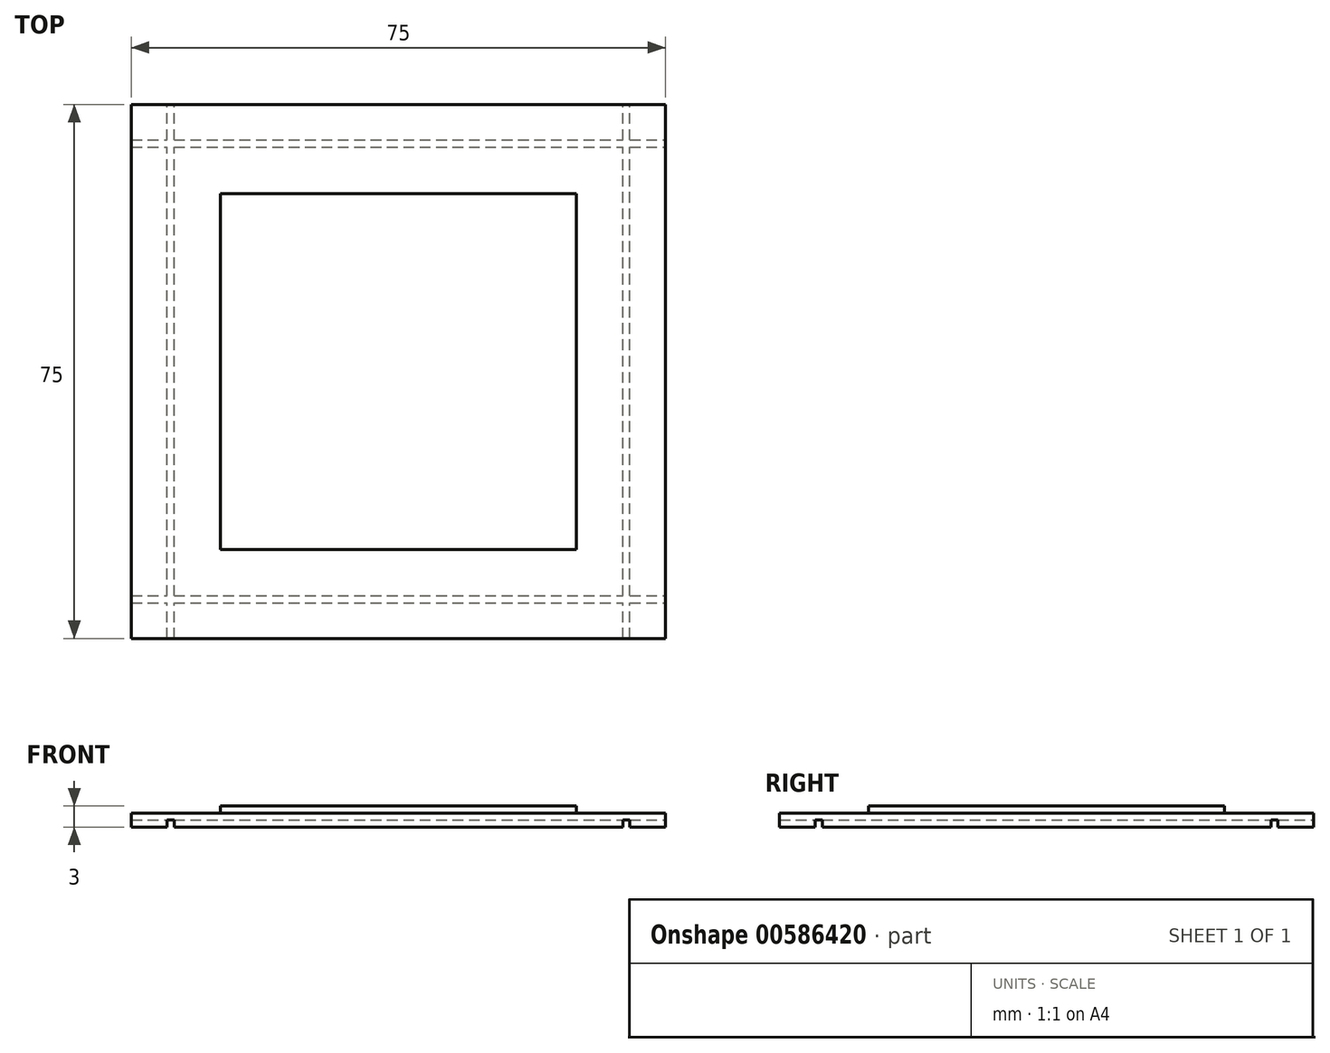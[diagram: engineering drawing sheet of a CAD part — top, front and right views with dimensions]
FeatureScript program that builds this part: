
annotation { "Feature Type Name" : "Feature", "Feature Type Description" : "" }
export const myFeature = defineFeature(function(context is Context, id is Id, definition is map)
    precondition{}
    {
        {
            var Q0;
            Q0=qCreatedBy(makeId("Top.planeOp"),FACE);
            var sketch = newSketch(context, id + "F0", { "sketchPlane" : qUnion([Q0])});
            skLineSegment(sketch, "E0.bottom", {"start": v(-37.5, -37.5) * mm, "end": v(37.5, -37.5) * mm});
            skLineSegment(sketch, "E0.top", {"start": v(-37.5, 37.5) * mm, "end": v(37.5, 37.5) * mm});
            skLineSegment(sketch, "E0.left", {"start": v(-37.5, -37.5) * mm, "end": v(-37.5, 37.5) * mm});
            skLineSegment(sketch, "E0.right", {"start": v(37.5, -37.5) * mm, "end": v(37.5, 37.5) * mm});
            skPoint(sketch, "E0.middle", {"position": v(0, 0) * mm});
            skLineSegment(sketch, "E1.bottom", {"start": v(-25, -25) * mm, "end": v(25, -25) * mm});
            skLineSegment(sketch, "E1.top", {"start": v(-25, 25) * mm, "end": v(25, 25) * mm});
            skLineSegment(sketch, "E1.left", {"start": v(-25, -25) * mm, "end": v(-25, 25) * mm});
            skLineSegment(sketch, "E1.right", {"start": v(25, -25) * mm, "end": v(25, 25) * mm});
            skSolve(sketch);
        }
        {
            var Q0;
            Q0=makeQuery(id+"F0.imprint","IMPRINT",FACE,{"disambiguationData":[TD([[makeQuery(id+"F0.imprint","IMPRINT",EDGE,{"derivedFrom":sQuery(id+"F0.wireOp",EDGE,"E1.bottom")}),1.0]])]});
            var Q1;
            Q1=makeQuery(id+"F0.imprint","IMPRINT",FACE,{"disambiguationData":[TD([[makeQuery(id+"F0.imprint","IMPRINT",EDGE,{"derivedFrom":sQuery(id+"F0.wireOp",EDGE,"E0.bottom")}),1.0]])]});
            extrude(context, id + "F1", {"entities" : qUnion([Q0, Q1]), "depth" : 2 * mm, "offsetDistance" : 25 * mm});
        }
        {
            var Q0;
            Q0=makeQuery(id+"F0.imprint","IMPRINT",FACE,{"disambiguationData":[TD([[makeQuery(id+"F0.imprint","IMPRINT",EDGE,{"derivedFrom":sQuery(id+"F0.wireOp",EDGE,"E1.bottom")}),1.0]])]});
            extrude(context, id + "F2", {"entities" : qUnion([Q0]), "operationType" : NewBodyOperationType.ADD, "depth" : 3 * mm, "offsetDistance" : 25 * mm});
        }
        {
            var Q0;
            Q0=makeQuery(id+"F0.imprint","IMPRINT",FACE,{"disambiguationData":[TD([[makeQuery(id+"F0.imprint","IMPRINT",EDGE,{"derivedFrom":sQuery(id+"F0.wireOp",EDGE,"E0.bottom")}),1.0]])]});
            var sketch = newSketch(context, id + "F3", { "sketchPlane" : qUnion([Q0])});
            skLineSegment(sketch, "E2.bottom", {"start": v(-32.5, -37.5) * mm, "end": v(-31.5, -37.5) * mm});
            skLineSegment(sketch, "E2.top", {"start": v(-32.5, 37.5) * mm, "end": v(-31.5, 37.5) * mm});
            skLineSegment(sketch, "E2.left", {"start": v(-32.5, -37.5) * mm, "end": v(-32.5, 37.5) * mm});
            skLineSegment(sketch, "E2.right", {"start": v(-31.5, -37.5) * mm, "end": v(-31.5, 37.5) * mm});
            skLineSegment(sketch, "E3.bottom", {"start": v(-37.5, -32.5) * mm, "end": v(37.5, -32.5) * mm});
            skLineSegment(sketch, "E3.top", {"start": v(-37.5, -31.5) * mm, "end": v(37.5, -31.5) * mm});
            skLineSegment(sketch, "E3.left", {"start": v(-37.5, -32.5) * mm, "end": v(-37.5, -31.5) * mm});
            skLineSegment(sketch, "E3.right", {"start": v(37.5, -32.5) * mm, "end": v(37.5, -31.5) * mm});
            skLineSegment(sketch, "E4.bottom", {"start": v(32.5, -37.5) * mm, "end": v(31.5, -37.5) * mm});
            skLineSegment(sketch, "E4.top", {"start": v(32.5, 37.5) * mm, "end": v(31.5, 37.5) * mm});
            skLineSegment(sketch, "E4.left", {"start": v(32.5, -37.5) * mm, "end": v(32.5, 37.5) * mm});
            skLineSegment(sketch, "E4.right", {"start": v(31.5, -37.5) * mm, "end": v(31.5, 37.5) * mm});
            skLineSegment(sketch, "E5.bottom", {"start": v(-37.5, 31.5) * mm, "end": v(37.5, 31.5) * mm});
            skLineSegment(sketch, "E5.top", {"start": v(-37.5, 32.5) * mm, "end": v(37.5, 32.5) * mm});
            skLineSegment(sketch, "E5.left", {"start": v(-37.5, 31.5) * mm, "end": v(-37.5, 32.5) * mm});
            skLineSegment(sketch, "E5.right", {"start": v(37.5, 31.5) * mm, "end": v(37.5, 32.5) * mm});
            skSolve(sketch);
        }
        {
            var Q0;
            Q0 = qSketchRegion(id + "F3", true);
            extrude(context, id + "F4", {"entities" : qUnion([Q0]), "operationType" : NewBodyOperationType.REMOVE, "depth" : 1 * mm, "offsetDistance" : 25 * mm});
        }
    });
